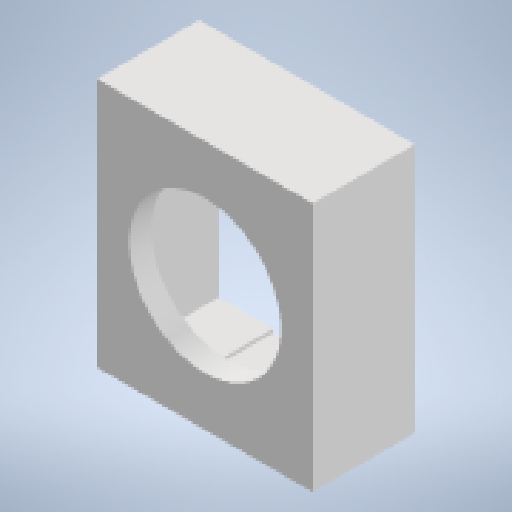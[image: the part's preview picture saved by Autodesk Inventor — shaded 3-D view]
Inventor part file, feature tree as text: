
AUTODESK INVENTOR PART (.ipt)
format: ipt  version: 2024.2 (Build 282272000, 272)  size: 252,928 bytes
history: native  units: mm
features: extrude x6, sketch x5, other x3, projected_geometry x2, plane x1, reference x1
ambient origin geometry x8: Origin, YZ Plane, XZ Plane, XY Plane, X Axis, Y Axis, Z Axis, Center Point
bodies: Solid1 (feature_tree)
feature tree (18):
  extrude  "Extrusion1"  Depth=4.0mm TaperAngle=0.0deg
  sketch  "Sketch2"  dims[d3=4.0mm d4=0.5mm]
  plane  "Work Plane1"
  extrude  "Extrusion2"  Depth=4.0mm
  extrude  "Extrusion3"  Depth=4.0mm TaperAngle=0.0deg
  extrude  "Extrusion4"  Depth=0.5mm TaperAngle=0.0deg
  extrude  "Extrusion5"  TaperAngle=0.0deg  [1 undecoded]
  extrude  "Extrusion6"  Depth=10.0mm
  sketch  "Sketch1"  dims[d0=2.0mm d1=4.0mm d2=0.0mm]
  reference  "Reference1"
  projected_geometry  "Projected Loop1"
  sketch  "Sketch3"  dims[d5=4.0mm d6=0.0mm d7=4.0mm d8=0.0mm]
  sketch  "Sketch4"  dims[d9=3.2mm d10=0.5mm d11=0.0mm]
  sketch  "Sketch5"  dims[d12=3.2mm d13=0.0mm d14=0.0mm d15=10.0mm d16=10.0mm d17=3.2mm d18=5.0mm d19=3.2mm d20=5.0mm d21=10.0mm d22=3.2mm d23=10.0mm d24=2.5mm d25=0.0mm]
  projected_geometry  "Projected Loop2"
  other  "<userpath>\Desktop\meca_robotbebou\Robotbebou.iam"
  other  "Robotbebou.iam"
  other  "Stop Switch Push Button LAY37 (PBC):1"
note: 1 required parameter value undecoded (feature->parameter linkage not recoverable at this tier; creation-order binding heuristic only, values carry confidence <= 0.55)
